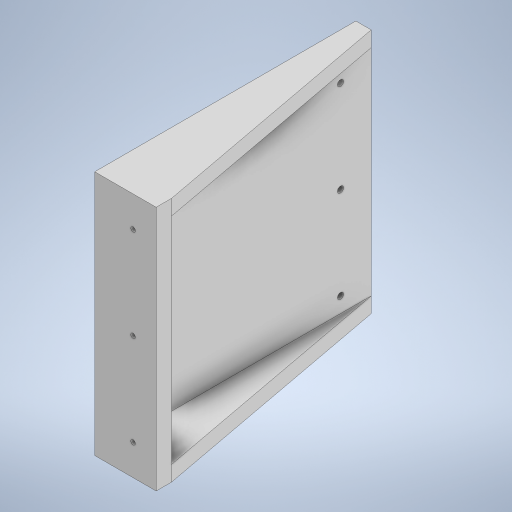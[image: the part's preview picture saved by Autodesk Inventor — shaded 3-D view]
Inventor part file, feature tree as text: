
AUTODESK INVENTOR PART (.ipt)
format: ipt  version: 2023 (Build 270158000, 158)  size: 313,344 bytes
history: native  units: mm
features: extrude x7, sketch x7
ambient origin geometry x8: Origin, YZ Plane, XZ Plane, XY Plane, X Axis, Y Axis, Z Axis, Center Point
bodies: Body1 (feature_tree)
feature tree (14):
  extrude  "Extrusion15"  Depth=160.0mm
  extrude  "Extrusion16"  Depth=170.0mm
  extrude  "Extrusion17"  Depth=10.0mm TaperAngle=0.0deg
  extrude  "Extrusion18"  Depth=10.0mm TaperAngle=0.0deg
  extrude  "Extrusion19"  Depth=3.0mm
  extrude  "Extrusion20"  Depth=20.0mm TaperAngle=0.0deg
  extrude  "Extrusion21"  Depth=4.0mm
  sketch  "Sketch21"  dims[d53=30.0mm d1=160.0mm]
  sketch  "Sketch22"  dims[d55=10.0mm d56=0.0mm d57=170.0mm]
  sketch  "Sketch23"  dims[d58=160.0mm d59=10.0mm d60=0.0mm]
  sketch  "Sketch24"  dims[d61=10.0mm d62=0.0mm d63=10.0mm d64=0.0mm]
  sketch  "Sketch25"  dims[d65=3.0mm d66=3.0mm]
  sketch  "Sketch27"  dims[d67=3.0mm d68=20.0mm d69=0.0mm]
  sketch  "Sketch29"  dims[d70=20.0mm d71=20.0mm d72=80.0mm d73=20.0mm d74=4.0mm d75=4.0mm d76=80.0mm d77=4.0mm d78=20.0mm d79=20.0mm d80=20.0mm d81=20.0mm d82=20.0mm d83=0.0mm d84=4.0mm d85=20.0mm d86=80.0mm d87=4.0mm d88=20.0mm d89=20.0mm d90=4.0mm d91=20.0mm d92=20.0mm d93=7.0mm d94=7.0mm d95=7.0mm d96=7.0mm d97=7.0mm d98=7.0mm d99=4.0mm d100=0.0mm d49=0.5mm d50=0.872665mm d51=0.5mm d52=0.872665mm]
